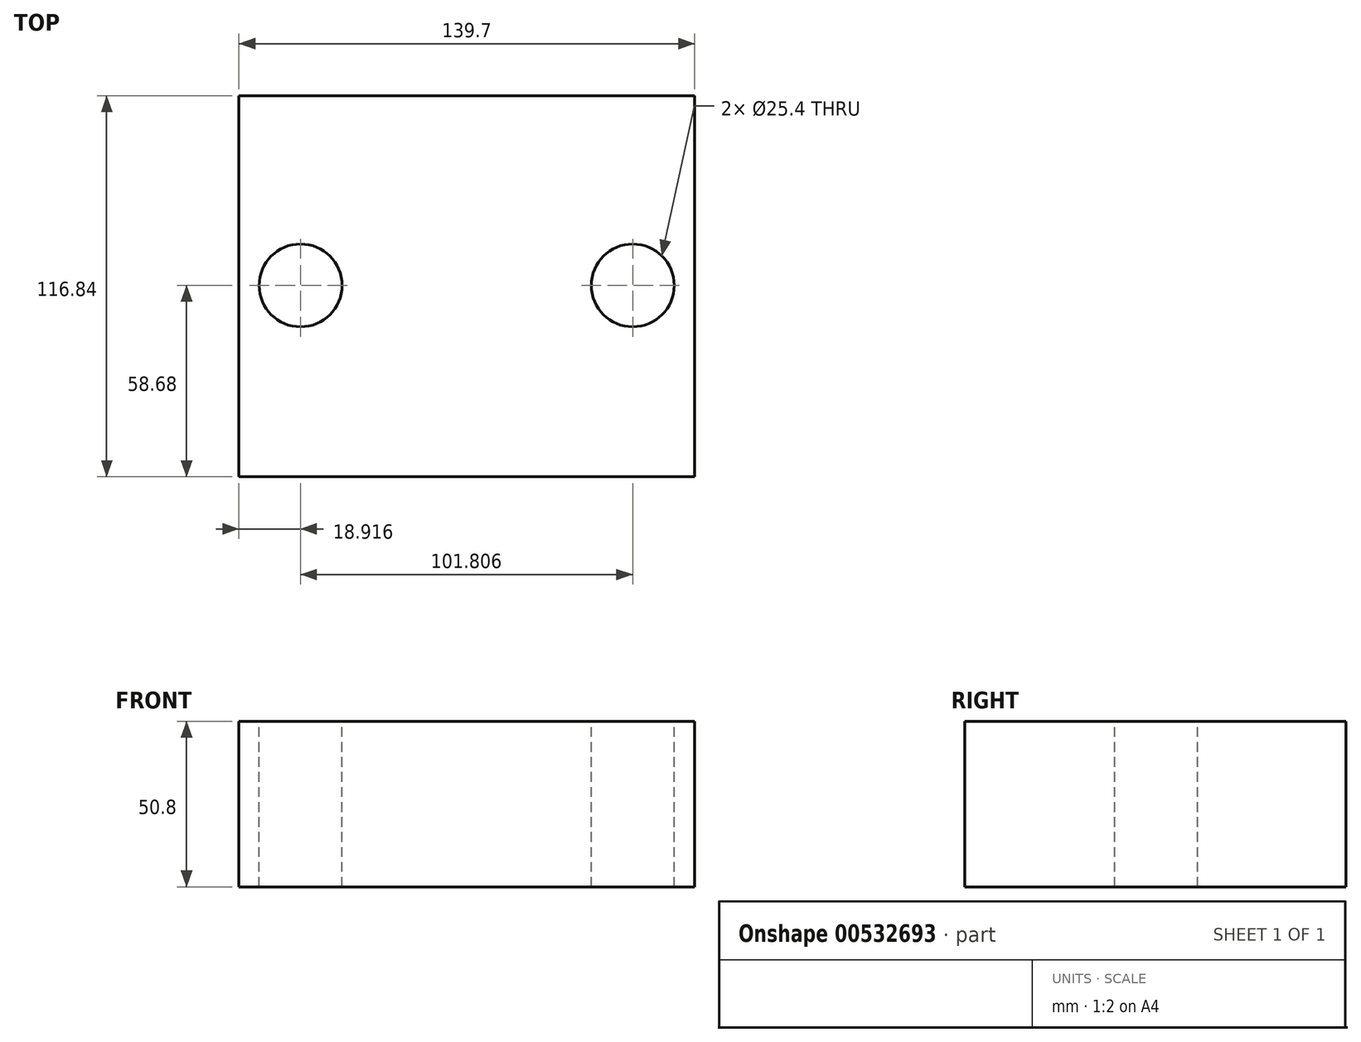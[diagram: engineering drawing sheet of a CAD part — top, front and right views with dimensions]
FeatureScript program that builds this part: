
annotation { "Feature Type Name" : "Feature", "Feature Type Description" : "" }
export const myFeature = defineFeature(function(context is Context, id is Id, definition is map)
    precondition{}
    {
        {
            var Q0;
            Q0=qCreatedBy(makeId("Top.planeOp"),FACE);
            var sketch = newSketch(context, id + "F0", { "sketchPlane" : qUnion([Q0])});
            skLineSegment(sketch, "E0.bottom", {"start": v(-80.2, 58.16) * mm, "end": v(59.5, 58.16) * mm});
            skLineSegment(sketch, "E0.top", {"start": v(-80.2, -58.68) * mm, "end": v(59.5, -58.68) * mm});
            skLineSegment(sketch, "E0.left", {"start": v(-80.2, 58.16) * mm, "end": v(-80.2, -58.68) * mm});
            skLineSegment(sketch, "E0.right", {"start": v(59.5, 58.16) * mm, "end": v(59.5, -58.68) * mm});
            skCircle(sketch, "E1", {"center": v(40.51, 0) * mm, "radius": 12.7 * mm});
            skCircle(sketch, "E2", {"center": v(-61.3, 0) * mm, "radius": 12.7 * mm});
            skLineSegment(sketch, "E3", {"start": v(-61.3, 0) * mm, "end": v(40.51, 0) * mm});
            skSolve(sketch);
        }
        {
            var Q0;
            Q0 = qSketchRegion(id + "F0", true);
            extrude(context, id + "F1", {"entities" : qUnion([Q0]), "oppositeDirection" : true, "depth" : 50.8 * mm, "offsetDistance" : 25.4 * mm});
        }
        {
            var Q0;
            Q0=sQuery(id+"F0.wireOp",EDGE,"E3");
            extrude(context, id + "F2", {"bodyType" : ToolBodyType.SURFACE, "surfaceEntities" : qUnion([Q0]), "depth" : 76.2 * mm, "offsetDistance" : 25.4 * mm});
        }
        {
            var Q0;
            Q0=makeQuery(id+"F2.opExtrude","SWEPT_FACE",FACE,{"disambiguationData":[OSD([sQuery(id+"F0.wireOp",EDGE,"E3")])]});
            var sketch = newSketch(context, id + "F3", { "sketchPlane" : qUnion([Q0])});
            skFitSpline(sketch, "E4", {"points": [v(-61.3, 0) * mm, v(-50.14, 41.06) * mm, v(-18.03, 52.78) * mm, v(0, 52.7) * mm, v(28.12, 47.73) * mm, v(40.51, 4.82) * mm, v(40.51, 0) * mm], "startDerivative": vector(15.18, 225.74) * mm, "endDerivative": vector(-3.05, -42.8) * mm});
            skSolve(sketch);
        }
        {
            var Q0;
            Q0=makeQuery(id+"F0.imprint","IMPRINT",FACE,{"disambiguationData":[TD([[makeQuery(id+"F0.imprint","IMPRINT",EDGE,{"derivedFrom":sQuery(id+"F0.wireOp",EDGE,"E2")}),1.0]])]});
            var Q1;
            Q1=makeQuery(id+"F0.imprint","IMPRINT",FACE,{"disambiguationData":[TD([[makeQuery(id+"F0.imprint","IMPRINT",EDGE,{"derivedFrom":sQuery(id+"F0.wireOp",EDGE,"E1")}),1.0]])]});
            var Q2;
            Q2=sQuery(id+"F0.wireOp",EDGE,"E2");
            var Q3;
            Q3=sQuery(id+"F3.wireOp",EDGE,"E4");
            sweep(context, id + "F4", {"bodyType" : ToolBodyType.SURFACE, "operationType" : NewBodyOperationType.INTERSECT, "profiles" : qUnion([Q0, Q1]), "surfaceProfiles" : qUnion([Q2]), "path" : qUnion([Q3])});
        }
        {
            var Q0;
            Q0=makeQuery(id+"F2.opExtrude","SWEPT_BODY",BODY,{"disambiguationData":[OSD([sQuery(id+"F0.wireOp",EDGE,"E3")])]});
            deleteBodies(context, id + "F5", {"entities" : qUnion([Q0])});
        }
    });
